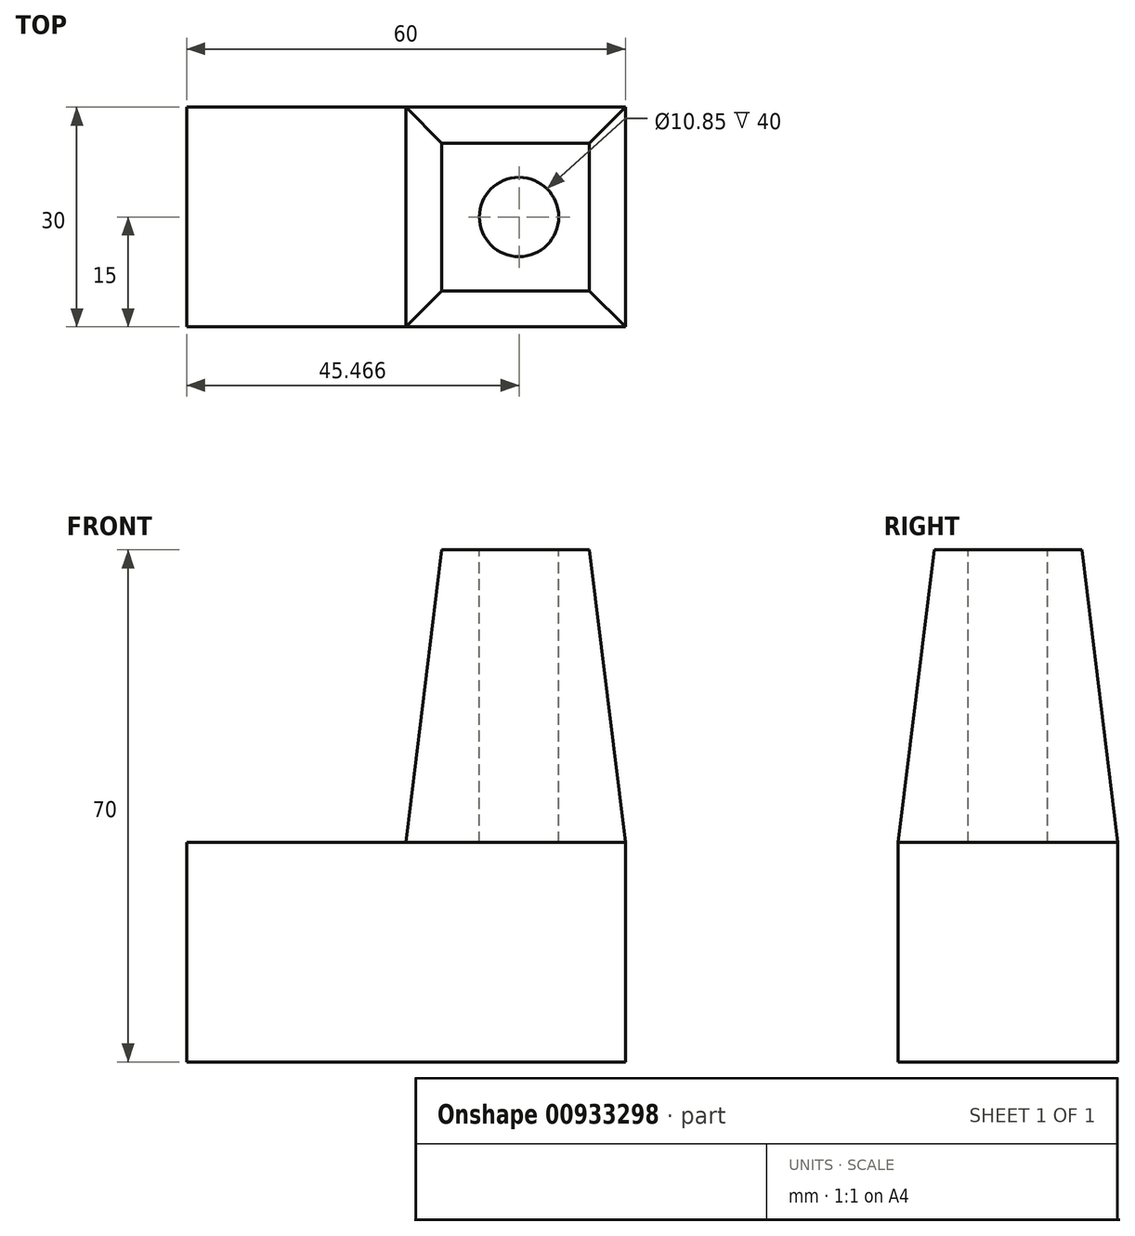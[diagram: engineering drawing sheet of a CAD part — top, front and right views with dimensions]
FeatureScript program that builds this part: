
annotation { "Feature Type Name" : "Feature", "Feature Type Description" : "" }
export const myFeature = defineFeature(function(context is Context, id is Id, definition is map)
    precondition{}
    {
        {
            var Q0;
            Q0=qCreatedBy(makeId("Front.planeOp"),FACE);
            var sketch = newSketch(context, id + "F0", { "sketchPlane" : qUnion([Q0])});
            skLineSegment(sketch, "E0.bottom", {"start": v(0, 0) * mm, "end": v(-60, 0) * mm});
            skLineSegment(sketch, "E0.top", {"start": v(0, -30) * mm, "end": v(-60, -30) * mm});
            skLineSegment(sketch, "E0.left", {"start": v(0, 0) * mm, "end": v(0, -30) * mm});
            skLineSegment(sketch, "E0.right", {"start": v(-60, 0) * mm, "end": v(-60, -30) * mm});
            skSolve(sketch);
        }
        {
            var Q0;
            Q0=makeQuery(id+"F0.imprint","IMPRINT",FACE,{"disambiguationData":[TD([[makeQuery(id+"F0.imprint","IMPRINT",EDGE,{"derivedFrom":sQuery(id+"F0.wireOp",EDGE,"E0.bottom")}),1.0]])]});
            extrude(context, id + "F1", {"entities" : qUnion([Q0]), "depth" : 30 * mm, "offsetDistance" : 25.4 * mm});
        }
        {
            var Q0;
            Q0=makeQuery(id+"F1.opExtrude","SWEPT_FACE",FACE,{"disambiguationData":[OSD([sQuery(id+"F0.wireOp",EDGE,"E0.bottom")])]});
            var sketch = newSketch(context, id + "F2", { "sketchPlane" : qUnion([Q0])});
            skLineSegment(sketch, "E1.bottom", {"start": v(-30, 0) * mm, "end": v(0, 0) * mm});
            skLineSegment(sketch, "E1.top", {"start": v(-30, -30) * mm, "end": v(0, -30) * mm});
            skLineSegment(sketch, "E1.left", {"start": v(-30, 0) * mm, "end": v(-30, -30) * mm});
            skLineSegment(sketch, "E1.right", {"start": v(0, 0) * mm, "end": v(0, -30) * mm});
            skSolve(sketch);
        }
        {
            var Q0;
            Q0=makeQuery(id+"F2.imprint","IMPRINT",FACE,{"disambiguationData":[TD([[makeQuery(id+"F2.imprint","IMPRINT",EDGE,{"derivedFrom":sQuery(id+"F2.wireOp",EDGE,"E1.bottom")}),1.0]])]});
            extrude(context, id + "F3", {"entities" : qUnion([Q0]), "operationType" : NewBodyOperationType.ADD, "depth" : 40 * mm, "offsetDistance" : 25.4 * mm, "hasDraft" : true, "draftAngle" : 7 * degree, "draftPullDirection" : true});
        }
        {
            var Q0;
            Q0=makeQuery(id+"F3.opExtrude","CAP_FACE",FACE,{"disambiguationData":[OSD([sQuery(id+"F2.wireOp",EDGE,"E1.bottom"),sQuery(id+"F2.wireOp",EDGE,"E1.top"),sQuery(id+"F2.wireOp",EDGE,"E1.left"),sQuery(id+"F2.wireOp",EDGE,"E1.right")])],"isStart":false});
            var sketch = newSketch(context, id + "F4", { "sketchPlane" : qUnion([Q0])});
            skCircle(sketch, "E2", {"center": v(-14.53, -15) * mm, "radius": 5.43 * mm});
            skPoint(sketch, "E2.centerSnap0", {"position": v(-25.09, -15) * mm});
            skSolve(sketch);
        }
        {
            var Q0;
            Q0 = qSketchRegion(id + "F4", true);
            extrude(context, id + "F5", {"entities" : qUnion([Q0]), "operationType" : NewBodyOperationType.REMOVE, "oppositeDirection" : true, "depth" : 40 * mm, "offsetDistance" : 25.4 * mm});
        }
    });
